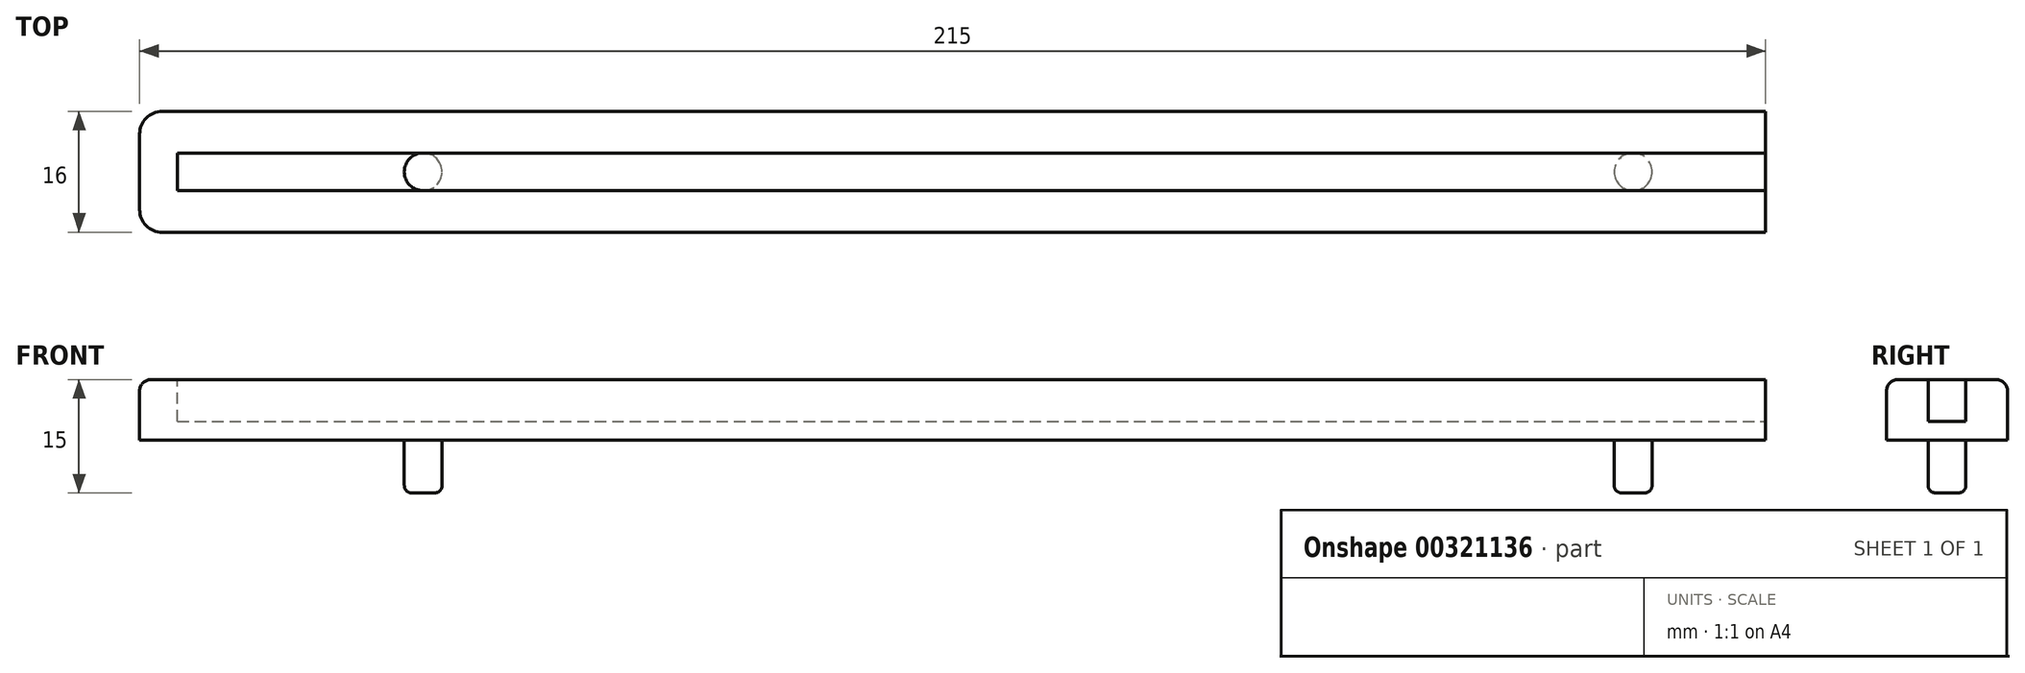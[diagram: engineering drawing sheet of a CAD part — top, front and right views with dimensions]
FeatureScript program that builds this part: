
annotation { "Feature Type Name" : "Feature", "Feature Type Description" : "" }
export const myFeature = defineFeature(function(context is Context, id is Id, definition is map)
    precondition{}
    {
        {
            var Q0;
            Q0=qCreatedBy(makeId("Top.planeOp"),FACE);
            var sketch = newSketch(context, id + "F0", { "sketchPlane" : qUnion([Q0])});
            skLineSegment(sketch, "E0.bottom", {"start": v(-115, 8) * mm, "end": v(100, 8) * mm});
            skLineSegment(sketch, "E0.top", {"start": v(-115, -8) * mm, "end": v(100, -8) * mm});
            skLineSegment(sketch, "E0.left", {"start": v(-115, 8) * mm, "end": v(-115, -8) * mm});
            skLineSegment(sketch, "E0.right", {"start": v(100, 8) * mm, "end": v(100, -8) * mm});
            skSolve(sketch);
        }
        {
            var Q0;
            Q0=makeQuery(id+"F0.imprint","IMPRINT",FACE,{"disambiguationData":[TD([[makeQuery(id+"F0.imprint","IMPRINT",EDGE,{"derivedFrom":sQuery(id+"F0.wireOp",EDGE,"E0.bottom")}),-1.0]])]});
            extrude(context, id + "F1", {"entities" : qUnion([Q0]), "depth" : 8 * mm});
        }
        {
            var Q0;
            Q0=makeQuery(id+"F1.opExtrude","CAP_FACE",FACE,{"disambiguationData":[OSD([sQuery(id+"F0.wireOp",EDGE,"E0.bottom"),sQuery(id+"F0.wireOp",EDGE,"E0.top"),sQuery(id+"F0.wireOp",EDGE,"E0.left"),sQuery(id+"F0.wireOp",EDGE,"E0.right")])],"isStart":true});
            var sketch = newSketch(context, id + "F2", { "sketchPlane" : qUnion([Q0])});
            skCircle(sketch, "E1", {"center": v(-77.5, 0) * mm, "radius": 2.5 * mm});
            skCircle(sketch, "E2", {"center": v(82.5, 0) * mm, "radius": 2.5 * mm});
            skSolve(sketch);
        }
        {
            var Q0;
            Q0 = qSketchRegion(id + "F2", true);
            extrude(context, id + "F3", {"entities" : qUnion([Q0]), "operationType" : NewBodyOperationType.ADD, "depth" : 7 * mm});
        }
        {
            var Q0;
            Q0=makeQuery(id+"F1.opExtrude","SWEPT_EDGE",EDGE,{"disambiguationData":[OSD([sQuery(id+"F0.wireOp",EDGE,"E0.top"),sQuery(id+"F0.wireOp",EDGE,"E0.left")])]});
            var Q1;
            Q1=makeQuery(id+"F1.opExtrude","SWEPT_EDGE",EDGE,{"disambiguationData":[OSD([sQuery(id+"F0.wireOp",EDGE,"E0.bottom"),sQuery(id+"F0.wireOp",EDGE,"E0.left")])]});
            fillet(context, id + "F4", {"entities" : qUnion([Q0, Q1]), "radius" : 3 * mm, "tangentPropagation" : true, "allowEdgeOverflow" : false});
        }
        {
            var Q0;
            Q0=makeQuery(id+"F3.opExtrude","CAP_EDGE",EDGE,{"disambiguationData":[OSD([sQuery(id+"F2.wireOp",EDGE,"E1")])],"isStart":false});
            var Q1;
            Q1=makeQuery(id+"F3.opExtrude","CAP_EDGE",EDGE,{"disambiguationData":[OSD([sQuery(id+"F2.wireOp",EDGE,"E2")])],"isStart":false});
            fillet(context, id + "F5", {"entities" : qUnion([Q0, Q1]), "radius" : 1 * mm, "tangentPropagation" : true, "allowEdgeOverflow" : false});
        }
        {
            var Q0;
            Q0=makeQuery(id+"F1.opExtrude","CAP_EDGE",EDGE,{"disambiguationData":[OSD([sQuery(id+"F0.wireOp",EDGE,"E0.top")])],"isStart":false});
            fillet(context, id + "F6", {"entities" : qUnion([Q0]), "radius" : 1.5 * mm, "tangentPropagation" : true, "allowEdgeOverflow" : false});
        }
        {
            var Q0;
            Q0=makeQuery(id+"F1.opExtrude","CAP_FACE",FACE,{"disambiguationData":[OSD([sQuery(id+"F0.wireOp",EDGE,"E0.bottom"),sQuery(id+"F0.wireOp",EDGE,"E0.top"),sQuery(id+"F0.wireOp",EDGE,"E0.left"),sQuery(id+"F0.wireOp",EDGE,"E0.right")])],"isStart":false});
            var sketch = newSketch(context, id + "F7", { "sketchPlane" : qUnion([Q0])});
            skLineSegment(sketch, "E3.bottom", {"start": v(-110, 2.5) * mm, "end": v(106.64, 2.5) * mm});
            skLineSegment(sketch, "E3.top", {"start": v(-110, -2.5) * mm, "end": v(106.64, -2.5) * mm});
            skLineSegment(sketch, "E3.left", {"start": v(-110, 2.5) * mm, "end": v(-110, -2.5) * mm});
            skLineSegment(sketch, "E3.right", {"start": v(106.64, 2.5) * mm, "end": v(106.64, -2.5) * mm});
            skLineSegment(sketch, "E4", {"start": v(-59.47, 0) * mm, "end": v(52.1, 0) * mm, "construction": true});
            skSolve(sketch);
        }
        {
            var Q0;
            {var subQ0=sQuery(id+"F7.wireOp",EDGE,"E3.left");Q0=makeQuery(id+"F7.imprint","IMPRINT",FACE,{"disambiguationData":[TD([[makeQuery(id+"F7.imprint","IMPRINT",EDGE,{"derivedFrom":subQ0}),1.0]])]});}
            extrude(context, id + "F8", {"entities" : qUnion([Q0]), "operationType" : NewBodyOperationType.REMOVE, "oppositeDirection" : true, "depth" : 5.5 * mm});
        }
    });
